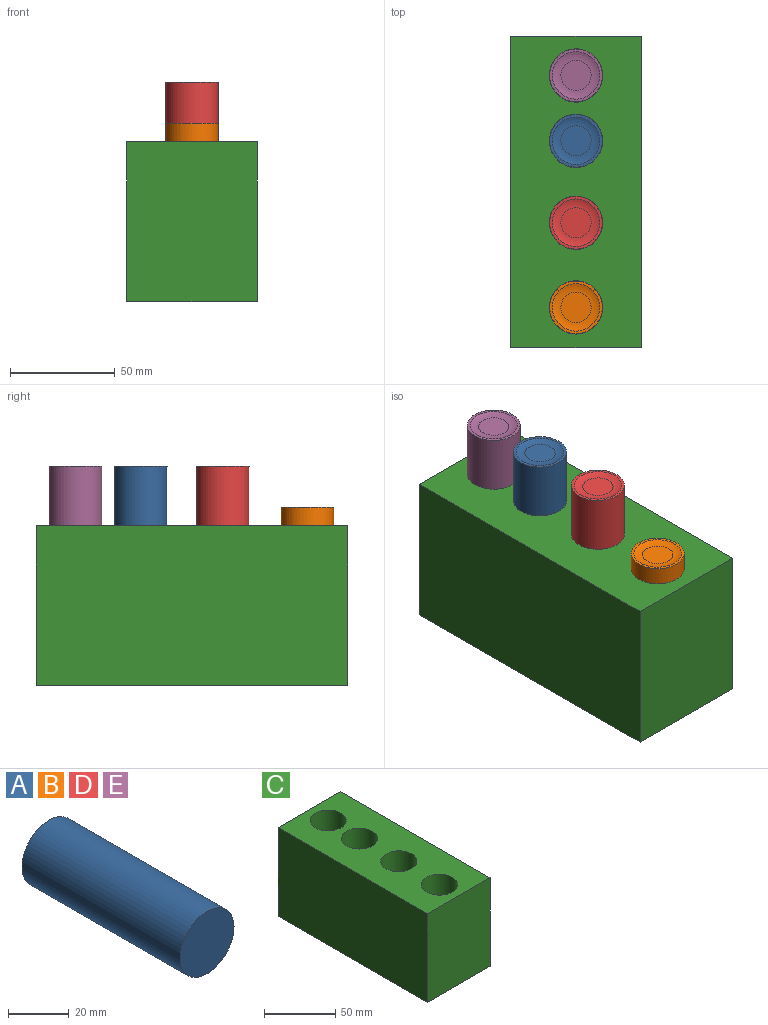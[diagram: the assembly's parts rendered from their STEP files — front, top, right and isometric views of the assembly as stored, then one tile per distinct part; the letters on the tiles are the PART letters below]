
ASSEMBLY  parts=5 mates=5
PART A: 5 faces, bbox 25.1x73.7x25.1 mm
  f0: cylinder r=12.57mm len=73.66mm, axis (0,1,0), area 5819mm2, adj f1,f2
  f1: plane 25.15x25.15mm, normal (0,-1,0), area 496.6mm2, adj f0
  f2: plane 25.15x25.15mm, normal (0,1,0), area 95.3mm2, adj f0,f4
  f3: plane 14.43x14.43mm, normal (0,1,0), area 163.6mm2, adj f4
  f4: torus R=7.22mm, axis (0,1,0), area 243.8mm2, adj f2,f3
PART B: same geometry as A
PART C: 10 faces, bbox 62.1x148.4x76.2 mm
  f0: plane 76.2x62.11mm, normal (0,-1,0), area 4733.1mm2, adj f1,f7,f8,f9
  f1: plane 148.38x76.2mm, normal (1,0,0), area 11306.6mm2, adj f0,f2,f8,f9
  f2: plane 76.2x62.11mm, normal (0,1,0), area 4733.1mm2, adj f1,f7,f8,f9
  f3: cylinder r=12.7mm len=76.2mm, axis (0,0,-1), area 6080.5mm2, adj f8,f9
  f4: cylinder r=12.7mm len=76.2mm, axis (0,0,-1), area 6080.5mm2, adj f8,f9
  f5: cylinder r=12.7mm len=76.2mm, axis (0,0,-1), area 6080.5mm2, adj f8,f9
  f6: cylinder r=12.7mm len=76.2mm, axis (0,0,-1), area 6080.5mm2, adj f8,f9
  f7: plane 148.38x76.2mm, normal (-1,0,0), area 11306.6mm2, adj f0,f2,f8,f9
  f8: plane 148.38x62.11mm, normal (0,0,1), area 7189.7mm2, adj f0,f1,f2,f3,f4,f5,f6,f7
  f9: plane 148.38x62.11mm, normal (0,0,-1), area 7189.7mm2, adj f0,f1,f2,f3,f4,f5,f6,f7
PART D: same geometry as A
PART E: same geometry as A
PLACE A rot(axis=(1,0,0),90deg) t=(-14.25,-39.29,22.89)mm
PLACE B rot(axis=(0,-0.71,-0.71),180deg) t=(-14.25,-118.64,3.29)mm
PLACE C t=(-14.25,-63.58,-30.85)mm
PLACE D rot(axis=(1,0,0),90deg) t=(-14.25,-78.32,22.89)mm
PLACE E rot(axis=(1,0,0),90deg) t=(-14.25,-8.13,22.89)mm
MATE cylindrical D.f0 <-> C.f5  axis (0,0,1) through (-14.25,-78.32,-13.94)mm
MATE cylindrical B.f0 <-> C.f6  axis (0,0,1) through (-14.25,-118.64,3.29)mm
MATE cylindrical E.f0 <-> C.f3  axis (0,0,1) through (-14.25,-8.13,-13.94)mm
MATE cylindrical B.f0 <-> C.f6  axis (0,0,1) through (-14.25,-118.64,-33.54)mm
MATE cylindrical A.f0 <-> C.f4  axis (0,0,1) through (-14.25,-39.29,-13.94)mm
